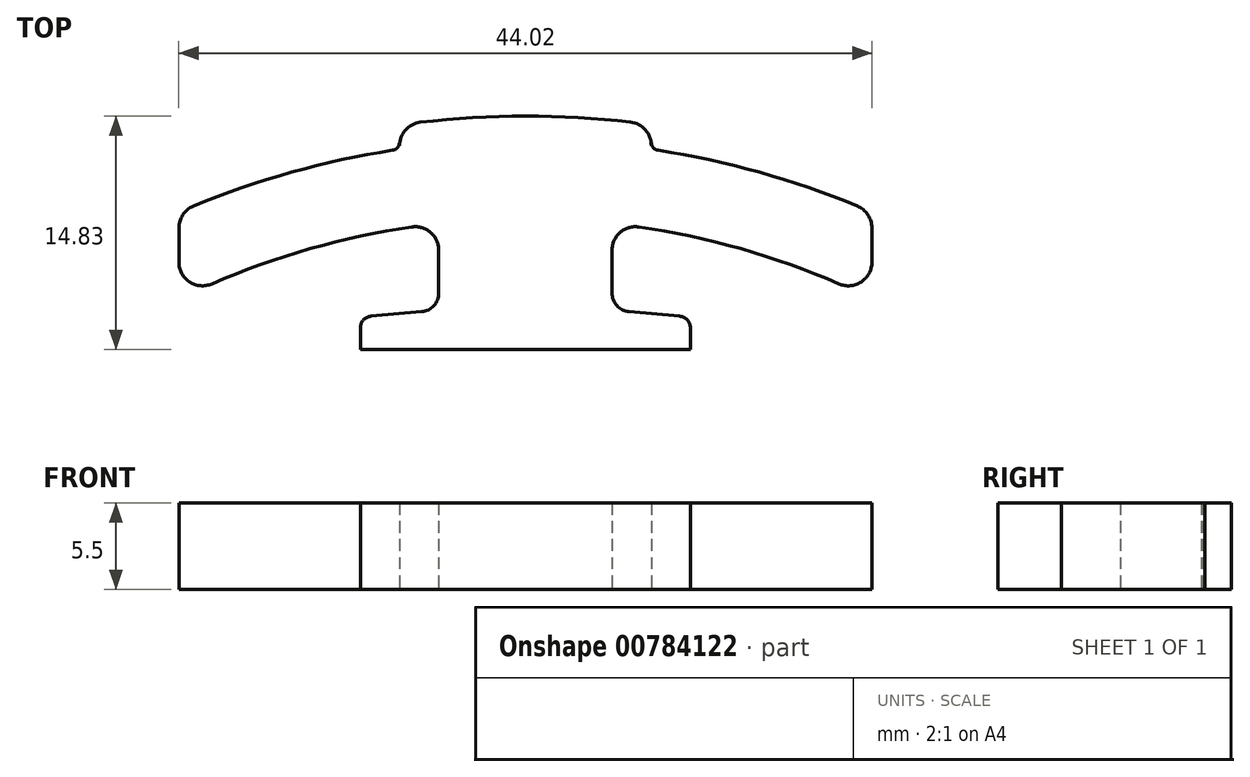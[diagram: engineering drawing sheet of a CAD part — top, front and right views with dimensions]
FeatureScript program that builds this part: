
annotation { "Feature Type Name" : "Feature", "Feature Type Description" : "" }
export const myFeature = defineFeature(function(context is Context, id is Id, definition is map)
    precondition{}
    {
        {
            var Q0;
            Q0=qCreatedBy(makeId("Top.planeOp"),FACE);
            var sketch = newSketch(context, id + "F0", { "sketchPlane" : qUnion([Q0])});
            skArc(sketch, "E0", {"start": v(-7.22, 49.39) * mm, "mid": v(-13.68, 48) * mm, "end": v(-19.91, 45.78) * mm});
            skLineSegment(sketch, "E1.left", {"start": v(5.5, 44.1) * mm, "end": v(5.5, 47.9) * mm});
            skLineSegment(sketch, "E1.right", {"start": v(-5.5, 44.1) * mm, "end": v(-5.5, 47.9) * mm});
            skArc(sketch, "E2.0", {"start": v(21.08, 50.71) * mm, "mid": v(14.86, 52.87) * mm, "end": v(8.42, 54.26) * mm});
            skLineSegment(sketch, "E3", {"start": v(-5.5, 41.6) * mm, "end": v(5.5, 41.6) * mm});
            skLineSegment(sketch, "E4", {"start": v(-22, 47.15) * mm, "end": v(-22, 49.33) * mm});
            skArc(sketch, "E5.trimOffspring", {"start": v(19.91, 45.78) * mm, "mid": v(13.68, 48) * mm, "end": v(7.22, 49.39) * mm});
            skPoint(sketch, "E6.orphan", {"position": v(21, 0) * mm});
            skPoint(sketch, "E7.start.orphan", {"position": v(-21, 0) * mm});
            skLineSegment(sketch, "E8", {"start": v(22, 49.33) * mm, "end": v(22, 47.15) * mm});
            skArc(sketch, "E9.2", {"start": v(6.68, 56.05) * mm, "mid": v(0, 56.44) * mm, "end": v(-6.68, 56.04) * mm});
            skLineSegment(sketch, "E10", {"start": v(-8, 54.76) * mm, "end": v(-8, 54.55) * mm});
            skLineSegment(sketch, "E11", {"start": v(8, 54.76) * mm, "end": v(8, 54.56) * mm});
            skArc(sketch, "E12.trimOffspring", {"start": v(-8.42, 54.26) * mm, "mid": v(-14.86, 52.87) * mm, "end": v(-21.08, 50.71) * mm});
            skPoint(sketch, "E13.visualSharp", {"position": v(8, 54.33) * mm});
            skArc(sketch, "E13.filletArc", {"start": v(8, 54.76) * mm, "mid": v(8.12, 54.43) * mm, "end": v(8.42, 54.26) * mm});
            skPoint(sketch, "E14.visualSharp", {"position": v(-8, 55.87) * mm});
            skArc(sketch, "E14.filletArc", {"start": v(-6.68, 56.04) * mm, "mid": v(-7.62, 55.55) * mm, "end": v(-8, 54.55) * mm});
            skPoint(sketch, "E15.visualSharp", {"position": v(-8, 54.33) * mm});
            skArc(sketch, "E15.filletArc", {"start": v(-8.42, 54.26) * mm, "mid": v(-8.12, 54.43) * mm, "end": v(-8, 54.76) * mm});
            skPoint(sketch, "E16.visualSharp", {"position": v(8, 55.88) * mm});
            skArc(sketch, "E16.filletArc", {"start": v(8, 54.56) * mm, "mid": v(7.62, 55.55) * mm, "end": v(6.68, 56.05) * mm});
            skPoint(sketch, "E17.visualSharp", {"position": v(22, 50.32) * mm});
            skArc(sketch, "E17.filletArc", {"start": v(22, 49.33) * mm, "mid": v(21.76, 50.16) * mm, "end": v(21.08, 50.71) * mm});
            skPoint(sketch, "E18.visualSharp", {"position": v(-22, 50.32) * mm});
            skArc(sketch, "E18.filletArc", {"start": v(-21.08, 50.71) * mm, "mid": v(-21.76, 50.16) * mm, "end": v(-22, 49.33) * mm});
            skPoint(sketch, "E19.visualSharp", {"position": v(-22, 44.8) * mm});
            skArc(sketch, "E19.filletArc", {"start": v(-22, 47.15) * mm, "mid": v(-21.33, 45.9) * mm, "end": v(-19.91, 45.78) * mm});
            skPoint(sketch, "E20.visualSharp", {"position": v(-5.5, 49.6) * mm});
            skArc(sketch, "E20.filletArc", {"start": v(-5.5, 47.9) * mm, "mid": v(-6.02, 49.04) * mm, "end": v(-7.22, 49.39) * mm});
            skPoint(sketch, "E21.visualSharp", {"position": v(5.5, 49.6) * mm});
            skArc(sketch, "E21.filletArc", {"start": v(7.22, 49.39) * mm, "mid": v(6.02, 49.04) * mm, "end": v(5.5, 47.9) * mm});
            skPoint(sketch, "E22.visualSharp", {"position": v(22, 44.8) * mm});
            skArc(sketch, "E22.filletArc", {"start": v(19.91, 45.78) * mm, "mid": v(21.33, 45.9) * mm, "end": v(22, 47.15) * mm});
            skLineSegment(sketch, "E23.bottom", {"start": v(5.5, 44.1) * mm, "end": v(9.8, 43.73) * mm});
            skLineSegment(sketch, "E23.top", {"start": v(5.5, 41.6) * mm, "end": v(10.48, 41.6) * mm});
            skLineSegment(sketch, "E23.left", {"start": v(5.5, 41.6) * mm, "end": v(5.5, 41.6) * mm});
            skLineSegment(sketch, "E23.right", {"start": v(10.48, 42.98) * mm, "end": v(10.48, 41.6) * mm});
            skPoint(sketch, "E24.visualSharp", {"position": v(10.48, 43.67) * mm});
            skArc(sketch, "E24.filletArc", {"start": v(10.48, 42.98) * mm, "mid": v(10.28, 43.49) * mm, "end": v(9.8, 43.73) * mm});
            skLineSegment(sketch, "E25.MirrorCS", {"start": v(-5.5, 44.1) * mm, "end": v(-9.8, 43.73) * mm});
            skArc(sketch, "E26.MirrorCS", {"start": v(-10.48, 42.98) * mm, "mid": v(-10.28, 43.49) * mm, "end": v(-9.8, 43.73) * mm});
            skLineSegment(sketch, "E27.MirrorCS", {"start": v(-5.5, 41.6) * mm, "end": v(-10.48, 41.6) * mm});
            skLineSegment(sketch, "E28.MirrorCS", {"start": v(-5.5, 41.6) * mm, "end": v(-5.5, 41.6) * mm});
            skPoint(sketch, "E29.MirrorP", {"position": v(-10.48, 43.67) * mm});
            skLineSegment(sketch, "E30.MirrorCS", {"start": v(-10.48, 42.98) * mm, "end": v(-10.48, 41.6) * mm});
            skSolve(sketch);
        }
        {
            var Q0;
            Q0=makeQuery(id+"F0.imprint","IMPRINT",FACE,{"disambiguationData":[TD([[makeQuery(id+"F0.imprint","IMPRINT",EDGE,{"derivedFrom":sQuery(id+"F0.wireOp",EDGE,"E0")}),-1.0]])]});
            extrude(context, id + "F1", {"entities" : qUnion([Q0]), "depth" : 5.5 * mm, "offsetDistance" : 25 * mm});
        }
        {
            var Q0;
            Q0=makeQuery(id+"F1.opExtrude","SWEPT_EDGE",EDGE,{"disambiguationData":[OSD([sQuery(id+"F0.wireOp",EDGE,"E1.left"),sQuery(id+"F0.wireOp",EDGE,"E23.bottom")])]});
            var Q1;
            Q1=makeQuery(id+"F1.opExtrude","SWEPT_EDGE",EDGE,{"disambiguationData":[OSD([sQuery(id+"F0.wireOp",EDGE,"E1.right"),sQuery(id+"F0.wireOp",EDGE,"E25.MirrorCS")])]});
            fillet(context, id + "F2", {"entities" : qUnion([Q0, Q1]), "radius" : 1.2 * mm, "tangentPropagation" : true, "allowEdgeOverflow" : false});
        }
    });
